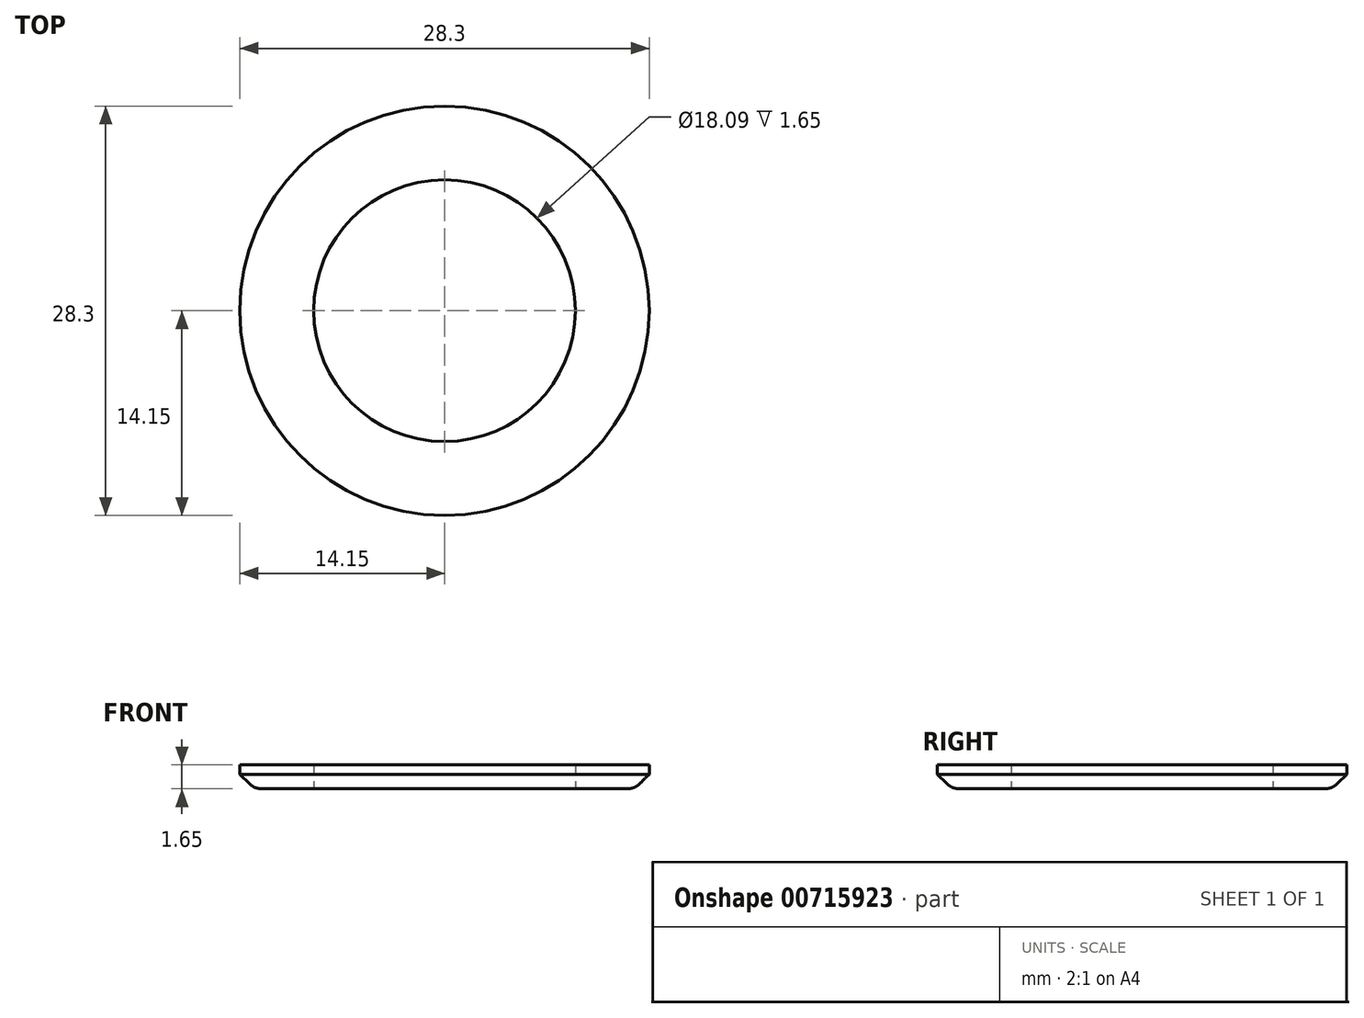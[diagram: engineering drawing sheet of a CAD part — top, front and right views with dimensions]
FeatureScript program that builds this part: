
annotation { "Feature Type Name" : "Feature", "Feature Type Description" : "" }
export const myFeature = defineFeature(function(context is Context, id is Id, definition is map)
    precondition{}
    {
        {
            var Q0;
            Q0=qCreatedBy(makeId("Top.planeOp"),FACE);
            var sketch = newSketch(context, id + "F0", { "sketchPlane" : qUnion([Q0])});
            skCircle(sketch, "E0", {"center": v(0, 0) * mm, "radius": 14.15 * mm});
            skCircle(sketch, "E1", {"center": v(0, 0) * mm, "radius": 9.05 * mm});
            skSolve(sketch);
        }
        {
            var Q0;
            Q0 = qSketchRegion(id + "F0", true);
            extrude(context, id + "F1", {"entities" : qUnion([Q0]), "depth" : 1.65 * mm, "offsetDistance" : 25 * mm});
        }
        {
            var Q0;
            Q0=makeQuery(id+"F1.opExtrude","CAP_EDGE",EDGE,{"disambiguationData":[OSD([sQuery(id+"F0.wireOp",EDGE,"E0")])],"isStart":true});
            chamfer(context, id + "F2", {"entities" : qUnion([Q0]), "width" : 1 * mm, "tangentPropagation" : true});
        }
        {
            var Q0;
            {var subQ0=sQuery(id+"F0.wireOp",EDGE,"E0");Q0=makeQuery(id+"F2.opChamfer","BLEND_EDGE",EDGE,{"blendedFrom":[makeQuery(id+"F1.opExtrude","CAP_EDGE",EDGE,{"disambiguationData":[OSD([subQ0])],"isStart":true}),makeQuery(id+"F1.opExtrude","CAP_FACE",FACE,{"disambiguationData":[OSD([subQ0,sQuery(id+"F0.wireOp",EDGE,"E1")])],"isStart":true})],"blendedInto":[makeQuery(id+"F1.opExtrude","CAP_FACE",FACE,{"disambiguationData":[OSD([subQ0,sQuery(id+"F0.wireOp",EDGE,"E1")])],"isStart":true})]});}
            fillet(context, id + "F3", {"entities" : qUnion([Q0]), "radius" : 1.2 * mm, "tangentPropagation" : true, "allowEdgeOverflow" : false});
        }
    });
